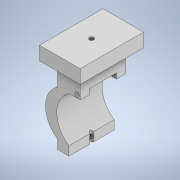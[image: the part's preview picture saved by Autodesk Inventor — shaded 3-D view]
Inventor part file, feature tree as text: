
AUTODESK INVENTOR PART (.ipt)
format: ipt  version: 2021 (Build 250183000, 183)  size: 188,928 bytes
history: native  units: in
note: dims shown in document units (in); Inventor stores cm internally (conversion verified against a paired STEP export)
features: sketch x7, extrude x5, hole x2
ambient origin geometry x8: Origin, YZ Plane, XZ Plane, XY Plane, X Axis, Y Axis, Z Axis, Center Point
bodies: Solid1 (feature_tree)
feature tree (14):
  extrude  "Extrusion1"  Depth=3.937in TaperAngle=0.0deg
  extrude  "Extrusion6"  Depth=3.937in
  extrude  "Extrusion7"  Depth=2.3622in
  hole  "Hole3"  [1 undecoded]
  extrude  "Extrusion8"  Depth=3.937in TaperAngle=0.0deg
  extrude  "Extrusion9"  Depth=1.9685in
  hole  "Hole4"  [1 undecoded]
  sketch  "Sketch2"  dims[d1=1.9685in d2=3.937in d3=0.0in]
  sketch  "Sketch12"  dims[d55=0.9843in d56=3.937in]
  sketch  "Sketch13"  dims[d57=1.9685in d58=2.3622in]
  sketch  "Sketch16"  dims[d59=0.7874in d60=2.3622in]
  sketch  "Sketch17"  dims[d61=0.9843in d62=3.937in d63=0.0in]
  sketch  "Sketch18"  dims[d68=0.9843in d69=1.9685in]
  sketch  "Sketch19"  dims[d70=5.5118in d71=3.5433in d72=1.1811in d73=0.0in d74=0.3937in d75=0.315in d76=0.2362in d77=0.3937in d78=0.1181in d79=90.0deg d80=0.315in d81=0.8108in d82=0.2756in d83=0.2756in d84=0.3937in d85=3.937in d86=0.0in d89=0.4724in d90=0.0in d91=0.3937in d92=0.3937in d93=0.3937in d94=0.2362in d95=0.3937in d96=0.1181in d97=90.0deg d98=0.315in d99=0.8108in d100=0.4724in d101=0.7874in d102=0.7874in d103=0.4724in d104=2.3622in d105=0.7874in d64=0.0197in d65=0.0344in d66=0.0197in d67=0.0344in]
note: 2 required parameter values undecoded (feature->parameter linkage not recoverable at this tier; creation-order binding heuristic only, values carry confidence <= 0.55)
